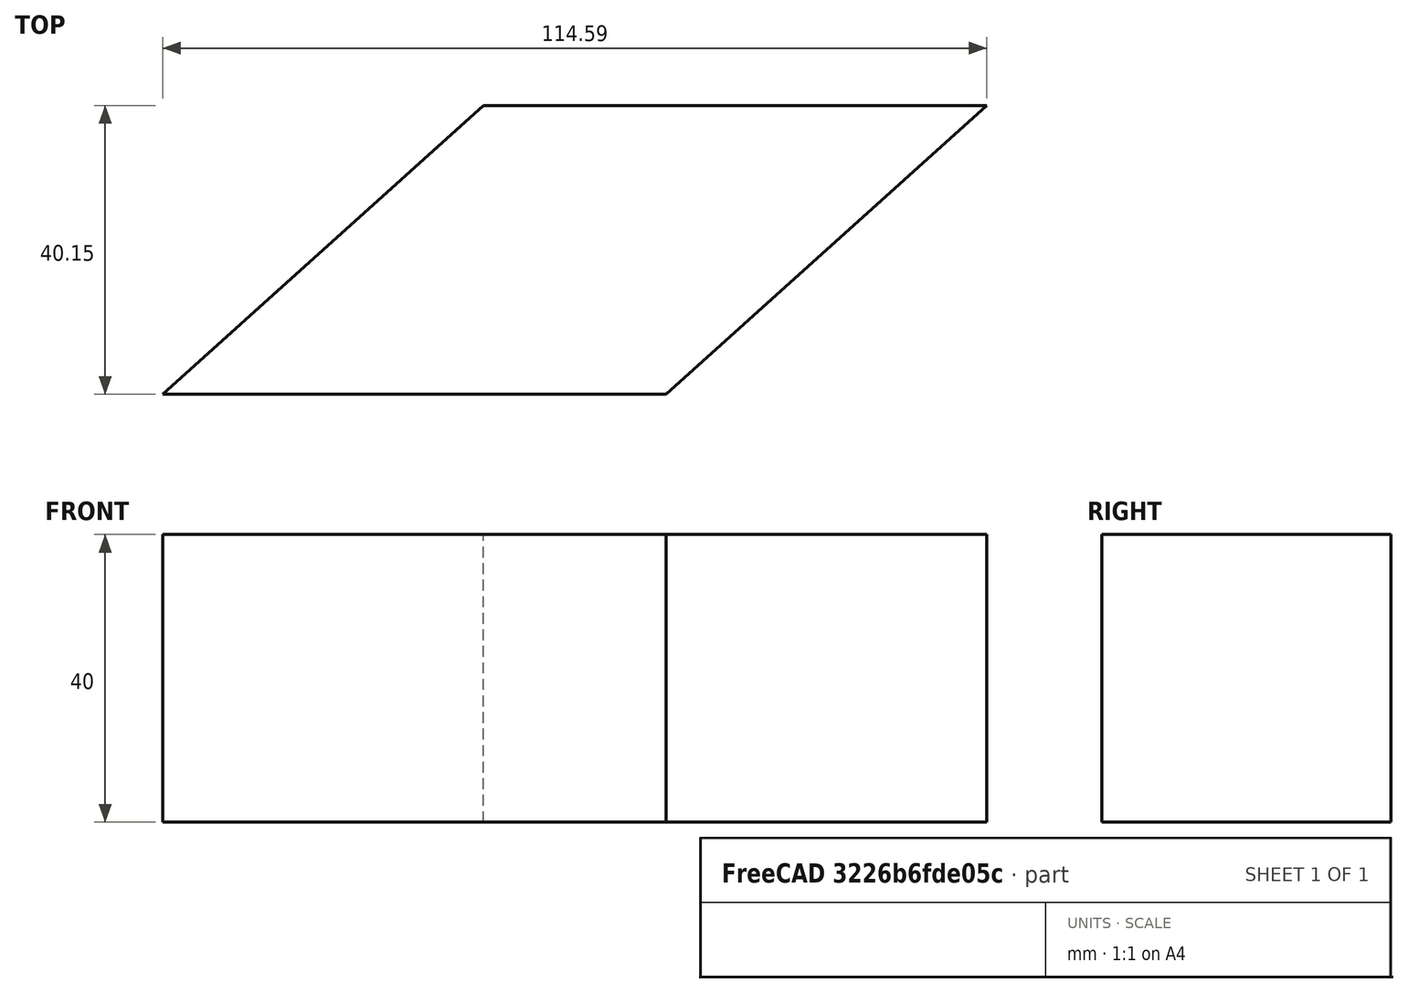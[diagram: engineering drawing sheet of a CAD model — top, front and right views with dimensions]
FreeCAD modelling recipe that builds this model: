
FCSTD DOCUMENT  (FreeCAD 0.19R)
Label: parallelogram
License: All rights reserved
LicenseURL: http://en.wikipedia.org/wiki/All_rights_reserved
objects: Sketcher::SketchObject×1, PartDesign::Pad×1, PartDesign::Body×1
note: 4 computed .brp shape members not serialized (recipe doc carries the construction recipe); baked Part::Feature solids carry a one-line shape summary decoded from their .brp

FEATURE [Sketcher::SketchObject] Sketch
  FullyConstrained = true
  MapMode = 5
  Support = -> [XY_Plane]
  sketch-geometry (4):
    g0: LineSegment StartX=52.5887 StartY=48.1478 StartZ=0 EndX=122.589 EndY=48.1478 EndZ=0
    g1: LineSegment StartX=122.589 StartY=48.1478 StartZ=0 EndX=78 EndY=8 EndZ=0
    g2: LineSegment StartX=78 StartY=8 StartZ=0 EndX=8 EndY=8 EndZ=0
    g3: LineSegment StartX=8 StartY=8 StartZ=0 EndX=52.5887 EndY=48.1478 EndZ=0
  constraints (12):
    c: Coincident(g0,g1)
    c: Coincident(g1,g2)
    c: Coincident(g2,g3)
    c: Coincident(g3,g0)
    c: Horizontal(g0)
    c: Horizontal(g2)
    c: DistanceX(g-1,g2) = 8
    c: DistanceY(g-1,g2) = 8
    c: Equal(g0,g2)
    c: DistanceX(g2,g1) = 70
    c: Angle(g2,g3) = 0.733038
    c: Distance(g1,g0) = 60
FEATURE [PartDesign::Pad] Pad
  Direction = (1,1,1)
  Length = 40
  Length2 = 100
  Profile = -> Sketch
  Type = 0
FEATURE [PartDesign::Body] Body
  Group = -> [Sketch,Pad]
  Origin = -> Origin
  Tip = -> Pad
